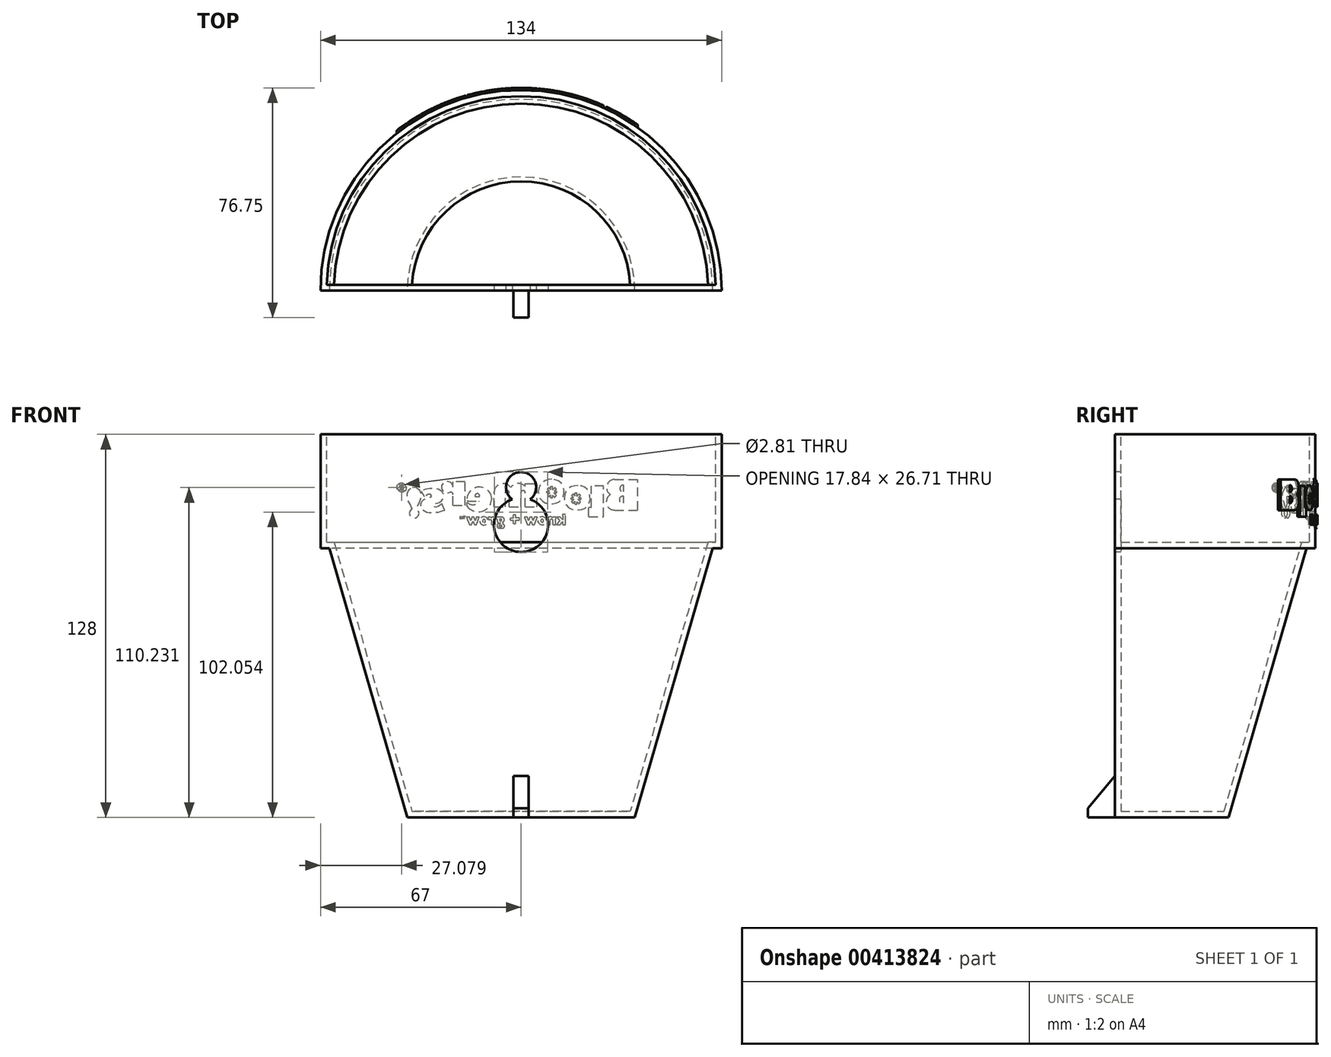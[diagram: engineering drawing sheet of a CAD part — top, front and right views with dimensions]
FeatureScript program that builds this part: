
annotation { "Feature Type Name" : "Feature", "Feature Type Description" : "" }
export const myFeature = defineFeature(function(context is Context, id is Id, definition is map)
    precondition{}
    {
        {
            var Q0;
            Q0=qCreatedBy(makeId("Front.planeOp"),FACE);
            var sketch = newSketch(context, id + "F0", { "sketchPlane" : qUnion([Q0])});
            skLineSegment(sketch, "E0", {"start": v(0, 56.42) * mm, "end": v(-67, 56.42) * mm});
            skLineSegment(sketch, "E1", {"start": v(-67, 56.42) * mm, "end": v(-67, 18.42) * mm});
            skLineSegment(sketch, "E2", {"start": v(0, -71.58) * mm, "end": v(-38, -71.58) * mm});
            skLineSegment(sketch, "E3", {"start": v(-67, 18.42) * mm, "end": v(-64, 18.42) * mm});
            skLineSegment(sketch, "E4", {"start": v(0, 56.42) * mm, "end": v(0, -71.58) * mm});
            skLineSegment(sketch, "E5", {"start": v(-64, 18.42) * mm, "end": v(-38, -71.58) * mm});
            skLineSegment(sketch, "E6.MirrorCS", {"start": v(0, 56.42) * mm, "end": v(67, 56.42) * mm});
            skLineSegment(sketch, "E7.MirrorCS", {"start": v(67, 56.42) * mm, "end": v(67, 18.42) * mm});
            skLineSegment(sketch, "E8.MirrorCS", {"start": v(67, 18.42) * mm, "end": v(64, 18.42) * mm});
            skLineSegment(sketch, "E9.MirrorCS", {"start": v(64, 18.42) * mm, "end": v(38, -71.58) * mm});
            skLineSegment(sketch, "E10.MirrorCS", {"start": v(0, -71.58) * mm, "end": v(38, -71.58) * mm});
            skSolve(sketch);
        }
        {
            var Q0;
            {var subQ0=sQuery(id+"F0.wireOp",EDGE,"E3");Q0=makeQuery(id+"F0.imprint","IMPRINT",FACE,{"disambiguationData":[TD([[makeQuery(id+"F0.imprint","IMPRINT",EDGE,{"derivedFrom":subQ0}),1.0]])]});}
            var Q1;
            {var subQ1=sQuery(id+"F0.wireOp",EDGE,"E0");Q1=makeQuery(id+"F0.imprint","IMPRINT",FACE,{"disambiguationData":[TD([[makeQuery(id+"F0.imprint","IMPRINT",EDGE,{"derivedFrom":subQ1}),1.0]])]});}
            var Q2;
            Q2=makeQuery(id+"F0.imprint","IMPRINT",FACE,{"disambiguationData":[TD([[makeQuery(id+"F0.imprint","IMPRINT",EDGE,{"derivedFrom":sQuery(id+"F0.wireOp",EDGE,"Kfnrekvc-ZjTY-c2iQ-cK4z-hKnBe4uEAVNk")}),1.0]])]});
            var Q3;
            Q3=sQuery(id+"F0.wireOp",EDGE,"E4");
            revolve(context, id + "F1", {"entities" : qUnion([Q0, Q1, Q2]), "axis" : qUnion([Q3]), "revolveType" : RevolveType.ONE_DIRECTION, "angle" : 180 * degree});
        }
        {
            var Q0;
            Q0=makeQuery(id+"FK2OT3XlAi37Aaq_1.splitOp","SPLIT",FACE,{"derivedFrom":makeQuery(id+"F1.opRevolve","SWEPT_FACE",FACE,{"disambiguationData":[OSD([sQuery(id+"F0.wireOp",EDGE,"E0")])]}),"isFromBackBody":true});
            shell(context, id + "F2", {"entities" : qUnion([Q0]), "thickness" : 2 * mm});
        }
        {
            var Q0;
            Q0=qCreatedBy(makeId("Front.planeOp"),FACE);
            var sketch = newSketch(context, id + "F3", { "sketchPlane" : qUnion([Q0])});
            skLineSegment(sketch, "E11.bottom", {"start": v(-2.5, -56.58) * mm, "end": v(2.5, -56.58) * mm});
            skLineSegment(sketch, "E11.top", {"start": v(-2.5, -71.58) * mm, "end": v(2.5, -71.58) * mm});
            skLineSegment(sketch, "E11.left", {"start": v(-2.5, -56.58) * mm, "end": v(-2.5, -71.58) * mm});
            skLineSegment(sketch, "E11.right", {"start": v(2.5, -56.58) * mm, "end": v(2.5, -71.58) * mm});
            skPoint(sketch, "E11.middle", {"position": v(0, -64.08) * mm});
            skSolve(sketch);
        }
        {
            var Q0;
            Q0=qSketchRegion(id+"F3",true);
            extrude(context, id + "F4", {"entities" : qUnion([Q0]), "operationType" : NewBodyOperationType.ADD, "depth" : 9 * mm});
        }
        {
            var Q0;
            Q0=qCreatedBy(makeId("Front.planeOp"),FACE);
            var sketch = newSketch(context, id + "F5", { "sketchPlane" : qUnion([Q0])});
            skCircle(sketch, "E12", {"center": v(0, 38.78) * mm, "radius": 5.05 * mm});
            skCircle(sketch, "E13", {"center": v(0, 26.17) * mm, "radius": 9.05 * mm});
            skSolve(sketch);
        }
        {
            var Q0;
            {var subQ0=sQuery(id+"F5.wireOp",EDGE,"E13");var subQ1=sQuery(id+"F5.wireOp",EDGE,"E12");var subQ2=makeQuery(id+"F5.imprint","INTERSECT",VERTEX,{"disambiguationData":[OD(0.0)],"derivedFrom":[subQ1,subQ0]});Q0=makeQuery(id+"F5.imprint","IMPRINT",FACE,{"disambiguationData":[TD([[makeQuery(id+"F5.imprint","IMPRINT",EDGE,{"disambiguationData":[TD([[subQ2,1.0]])],"derivedFrom":subQ1}),1.0]])]});}
            var Q1;
            {var subQ0=sQuery(id+"F5.wireOp",EDGE,"E13");var subQ1=sQuery(id+"F5.wireOp",EDGE,"E12");var subQ2=makeQuery(id+"F5.imprint","INTERSECT",VERTEX,{"disambiguationData":[OD(0.0)],"derivedFrom":[subQ1,subQ0]});Q1=makeQuery(id+"F5.imprint","IMPRINT",FACE,{"disambiguationData":[TD([[makeQuery(id+"F5.imprint","IMPRINT",EDGE,{"disambiguationData":[TD([[subQ2,-1.0]])],"derivedFrom":subQ1}),-1.0]])]});}
            var Q2;
            {var subQ0=sQuery(id+"F5.wireOp",EDGE,"E13");var subQ1=sQuery(id+"F5.wireOp",EDGE,"E12");var subQ2=makeQuery(id+"F5.imprint","INTERSECT",VERTEX,{"disambiguationData":[OD(0.0)],"derivedFrom":[subQ1,subQ0]});Q2=makeQuery(id+"F5.imprint","IMPRINT",FACE,{"disambiguationData":[TD([[makeQuery(id+"F5.imprint","IMPRINT",EDGE,{"disambiguationData":[TD([[subQ2,-1.0]])],"derivedFrom":subQ1}),1.0]])]});}
            var Q3;
            Q3=sQuery(id+"F5.wireOp",EDGE,"E12");
            var Q4;
            Q4=sQuery(id+"F5.wireOp",EDGE,"E13");
            extrude(context, id + "F6", {"entities" : qUnion([Q0, Q1, Q2]), "operationType" : NewBodyOperationType.REMOVE, "surfaceEntities" : qUnion([Q3, Q4]), "oppositeDirection" : true, "depth" : 10 * mm});
        }
        {
            var Q0;
            Q0=makeQuery(id+"F4.opExtrude","CAP_EDGE",EDGE,{"disambiguationData":[OSD([sQuery(id+"F3.wireOp",EDGE,"E11.bottom")])],"isStart":false});
            chamfer(context, id + "F7", {"entities" : qUnion([Q0]), "chamferType" : ChamferType.OFFSET_ANGLE, "width" : 10 * mm, "oppositeDirection" : false, "angle" : 50 * degree, "tangentPropagation" : true});
        }
        {
            var Q0;
            Q0=makeQuery(id+"F2.opShell","OFFSET_FACE",FACE,{"disambiguationData":[OSD([sQuery(id+"F0.wireOp",EDGE,"E0"),sQuery(id+"F0.wireOp",EDGE,"E1"),sQuery(id+"F0.wireOp",EDGE,"E2"),sQuery(id+"F0.wireOp",EDGE,"E3"),sQuery(id+"F0.wireOp",EDGE,"E4"),sQuery(id+"F0.wireOp",EDGE,"E5")])]});
            cPlane(context, id + "F8", {"entities" : qUnion([Q0]), "cplaneType" : CPlaneType.OFFSET, "offset" : 66.8 * mm, "width" : 150 * mm, "height" : 150 * mm});
        }
        {
            var Q0;
            Q0=qCreatedBy(id+"F8.planeOp",FACE);
            var sketch = newSketch(context, id + "F9", { "sketchPlane" : qUnion([Q0])});
            skLineSegment(sketch, "E14", {"start": v(-38.93, 41.35) * mm, "end": v(-38.93, 31.1) * mm});
            skLineSegment(sketch, "E15", {"start": v(-38.93, 31.1) * mm, "end": v(-31.26, 31.1) * mm});
            skLineSegment(sketch, "E16", {"start": v(-38.93, 41.35) * mm, "end": v(-31.26, 41.35) * mm});
            skArc(sketch, "E17", {"start": v(-29.86, 36.3) * mm, "mid": v(-28.64, 39.36) * mm, "end": v(-31.26, 41.35) * mm});
            skArc(sketch, "E18", {"start": v(-31.26, 31.1) * mm, "mid": v(-28.56, 33.17) * mm, "end": v(-29.86, 36.3) * mm});
            skLineSegment(sketch, "E19", {"start": v(-34.3, 39.39) * mm, "end": v(-34.3, 37.24) * mm});
            skArc(sketch, "E20", {"start": v(-34.3, 37.24) * mm, "mid": v(-33, 38.32) * mm, "end": v(-34.3, 39.39) * mm});
            skArc(sketch, "E21", {"start": v(-34.3, 33.47) * mm, "mid": v(-32.82, 34.59) * mm, "end": v(-34.3, 35.7) * mm});
            skLineSegment(sketch, "E22.trimOffspring", {"start": v(-34.3, 35.7) * mm, "end": v(-34.3, 33.47) * mm});
            skLineSegment(sketch, "E23", {"start": v(-27.58, 39.2) * mm, "end": v(-27.58, 28.9) * mm});
            skLineSegment(sketch, "E24", {"start": v(-27.58, 28.9) * mm, "end": v(-22.58, 28.9) * mm});
            skLineSegment(sketch, "E25", {"start": v(-22.58, 28.9) * mm, "end": v(-22.58, 31.98) * mm});
            skLineSegment(sketch, "E26", {"start": v(-22.58, 31.98) * mm, "end": v(-23.52, 31.98) * mm});
            skLineSegment(sketch, "E27", {"start": v(-23.52, 31.98) * mm, "end": v(-23.52, 39.2) * mm});
            skLineSegment(sketch, "E28", {"start": v(-23.52, 39.2) * mm, "end": v(-27.58, 39.2) * mm});
            skFitSpline(sketch, "E29", {"points": [v(-18.97, 39.3) * mm, v(-20.87, 38.92) * mm, v(-22.46, 37.44) * mm, v(-22.99, 35.82) * mm, v(-22.97, 34.09) * mm, v(-22.03, 32.34) * mm, v(-20.21, 31.27) * mm, v(-18.57, 31.14) * mm, v(-16.6, 31.5) * mm, v(-14.9, 33.15) * mm, v(-14.42, 35.37) * mm, v(-14.96, 37.3) * mm, v(-16.45, 38.75) * mm, v(-18.2, 39.28) * mm, v(-18.97, 39.3) * mm]});
            skLineSegment(sketch, "E30.bottom", {"start": v(-18.65, 36.9) * mm, "end": v(-18, 36.9) * mm});
            skLineSegment(sketch, "E30.top", {"start": v(-18.65, 33.13) * mm, "end": v(-18, 33.13) * mm});
            skLineSegment(sketch, "E30.left", {"start": v(-18.65, 36.9) * mm, "end": v(-18.65, 35.74) * mm});
            skLineSegment(sketch, "E30.right", {"start": v(-18, 36.9) * mm, "end": v(-18, 35.82) * mm});
            skLineSegment(sketch, "E31.bottom", {"start": v(-20.04, 35.3) * mm, "end": v(-19.23, 35.3) * mm});
            skLineSegment(sketch, "E31.top", {"start": v(-20.04, 34.7) * mm, "end": v(-19.05, 34.7) * mm});
            skLineSegment(sketch, "E31.left", {"start": v(-20.04, 35.3) * mm, "end": v(-20.04, 34.7) * mm});
            skLineSegment(sketch, "E31.right", {"start": v(-16.69, 35.3) * mm, "end": v(-16.69, 34.7) * mm});
            skLineSegment(sketch, "E32", {"start": v(-19.87, 35.97) * mm, "end": v(-19.23, 35.3) * mm});
            skLineSegment(sketch, "E33", {"start": v(-17.4, 33.43) * mm, "end": v(-16.88, 33.92) * mm});
            skLineSegment(sketch, "E34", {"start": v(-19.35, 36.45) * mm, "end": v(-19.87, 35.97) * mm});
            skLineSegment(sketch, "E35", {"start": v(-19.87, 33.85) * mm, "end": v(-19.25, 33.22) * mm});
            skLineSegment(sketch, "E36", {"start": v(-19.25, 33.22) * mm, "end": v(-18.65, 33.9) * mm});
            skLineSegment(sketch, "E37", {"start": v(-16.84, 35.97) * mm, "end": v(-17.39, 36.45) * mm});
            skLineSegment(sketch, "E38", {"start": v(-17.39, 36.45) * mm, "end": v(-18, 35.82) * mm});
            skLineSegment(sketch, "E39.trimOffspring", {"start": v(-18.65, 35.74) * mm, "end": v(-19.35, 36.45) * mm});
            skLineSegment(sketch, "E40.trimOffspring", {"start": v(-19.05, 34.7) * mm, "end": v(-19.87, 33.85) * mm});
            skLineSegment(sketch, "E41.trimOffspring", {"start": v(-18, 34.04) * mm, "end": v(-17.4, 33.43) * mm});
            skLineSegment(sketch, "E42.trimOffspring", {"start": v(-18.65, 33.9) * mm, "end": v(-18.65, 33.13) * mm});
            skLineSegment(sketch, "E43.trimOffspring", {"start": v(-18, 34.04) * mm, "end": v(-18, 33.13) * mm});
            skLineSegment(sketch, "E44.trimOffspring", {"start": v(-17.42, 35.3) * mm, "end": v(-16.84, 35.97) * mm});
            skLineSegment(sketch, "E45.trimOffspring", {"start": v(-17.42, 35.3) * mm, "end": v(-16.69, 35.3) * mm});
            skLineSegment(sketch, "E46.trimOffspring", {"start": v(-17.65, 34.7) * mm, "end": v(-16.69, 34.7) * mm});
            skFitSpline(sketch, "E47", {"points": [v(-10.3, 41.42) * mm, v(-12.2, 41.04) * mm, v(-13.79, 39.56) * mm, v(-14.32, 37.94) * mm, v(-14.3, 36.2) * mm, v(-13.36, 34.46) * mm, v(-11.55, 33.39) * mm, v(-9.9, 33.26) * mm, v(-7.94, 33.62) * mm, v(-6.23, 35.27) * mm, v(-5.76, 37.49) * mm, v(-6.3, 39.41) * mm, v(-7.79, 40.86) * mm, v(-9.54, 41.4) * mm, v(-10.3, 41.42) * mm]});
            skLineSegment(sketch, "E48", {"start": v(-17.65, 34.7) * mm, "end": v(-16.88, 33.92) * mm});
            skLineSegment(sketch, "E49.bottom", {"start": v(-10.58, 39.06) * mm, "end": v(-9.92, 39.06) * mm});
            skLineSegment(sketch, "E49.top", {"start": v(-10.58, 35.28) * mm, "end": v(-9.92, 35.28) * mm});
            skLineSegment(sketch, "E49.left", {"start": v(-10.58, 39.06) * mm, "end": v(-10.58, 37.9) * mm});
            skLineSegment(sketch, "E49.right", {"start": v(-9.92, 39.06) * mm, "end": v(-9.92, 37.97) * mm});
            skLineSegment(sketch, "E50.bottom", {"start": v(-11.97, 37.46) * mm, "end": v(-11.15, 37.46) * mm});
            skLineSegment(sketch, "E50.top", {"start": v(-11.97, 36.86) * mm, "end": v(-10.98, 36.86) * mm});
            skLineSegment(sketch, "E50.left", {"start": v(-11.97, 37.46) * mm, "end": v(-11.97, 36.86) * mm});
            skLineSegment(sketch, "E50.right", {"start": v(-8.61, 37.46) * mm, "end": v(-8.61, 36.86) * mm});
            skLineSegment(sketch, "E51", {"start": v(-11.8, 38.12) * mm, "end": v(-11.15, 37.46) * mm});
            skLineSegment(sketch, "E52", {"start": v(-9.32, 35.58) * mm, "end": v(-8.81, 36.08) * mm});
            skLineSegment(sketch, "E53", {"start": v(-11.27, 38.6) * mm, "end": v(-11.8, 38.12) * mm});
            skLineSegment(sketch, "E54", {"start": v(-11.8, 36) * mm, "end": v(-11.18, 35.37) * mm});
            skLineSegment(sketch, "E55", {"start": v(-11.18, 35.37) * mm, "end": v(-10.58, 36.05) * mm});
            skLineSegment(sketch, "E56", {"start": v(-8.76, 38.12) * mm, "end": v(-9.31, 38.6) * mm});
            skLineSegment(sketch, "E57", {"start": v(-9.31, 38.6) * mm, "end": v(-9.92, 37.97) * mm});
            skLineSegment(sketch, "E58.trimOffspring", {"start": v(-10.58, 37.9) * mm, "end": v(-11.27, 38.6) * mm});
            skLineSegment(sketch, "E59.trimOffspring", {"start": v(-10.98, 36.86) * mm, "end": v(-11.8, 36) * mm});
            skLineSegment(sketch, "E60.trimOffspring", {"start": v(-9.92, 36.2) * mm, "end": v(-9.32, 35.58) * mm});
            skLineSegment(sketch, "E61.trimOffspring", {"start": v(-10.58, 36.05) * mm, "end": v(-10.58, 35.28) * mm});
            skLineSegment(sketch, "E62.trimOffspring", {"start": v(-9.92, 36.2) * mm, "end": v(-9.92, 35.28) * mm});
            skLineSegment(sketch, "E63.trimOffspring", {"start": v(-9.34, 37.46) * mm, "end": v(-8.76, 38.12) * mm});
            skLineSegment(sketch, "E64.trimOffspring", {"start": v(-9.34, 37.46) * mm, "end": v(-8.61, 37.46) * mm});
            skLineSegment(sketch, "E65.trimOffspring", {"start": v(-9.58, 36.86) * mm, "end": v(-8.61, 36.86) * mm});
            skLineSegment(sketch, "E66", {"start": v(-9.58, 36.86) * mm, "end": v(-8.81, 36.08) * mm});
            skLineSegment(sketch, "E67", {"start": v(-5.38, 32.17) * mm, "end": v(-5.38, 39.97) * mm});
            skLineSegment(sketch, "E68", {"start": v(-5.38, 39.97) * mm, "end": v(-1.39, 39.97) * mm});
            skLineSegment(sketch, "E69", {"start": v(-1.39, 39.97) * mm, "end": v(-1.39, 39) * mm});
            skLineSegment(sketch, "E70", {"start": v(-5.38, 32.17) * mm, "end": v(-1.38, 32.17) * mm});
            skLineSegment(sketch, "E71", {"start": v(-1.38, 32.17) * mm, "end": v(-1.38, 36.98) * mm});
            skLineSegment(sketch, "E72", {"start": v(0, 36.98) * mm, "end": v(0, 32.17) * mm});
            skLineSegment(sketch, "E73", {"start": v(0, 32.17) * mm, "end": v(3.95, 32.17) * mm});
            skLineSegment(sketch, "E74", {"start": v(3.95, 32.17) * mm, "end": v(3.95, 36.98) * mm});
            skLineSegment(sketch, "E75", {"start": v(5.25, 36.98) * mm, "end": v(5.25, 32.17) * mm});
            skLineSegment(sketch, "E76", {"start": v(5.25, 32.17) * mm, "end": v(9.02, 32.17) * mm});
            skLineSegment(sketch, "E77", {"start": v(9.02, 32.17) * mm, "end": v(9.02, 36.98) * mm});
            skArc(sketch, "E78", {"start": v(5.25, 36.98) * mm, "mid": v(4.6, 37.63) * mm, "end": v(3.95, 36.98) * mm});
            skArc(sketch, "E79", {"start": v(0, 36.98) * mm, "mid": v(-0.69, 37.67) * mm, "end": v(-1.38, 36.98) * mm});
            skArc(sketch, "E80", {"start": v(3.53, 38.66) * mm, "mid": v(1.15, 40.01) * mm, "end": v(-1.39, 39) * mm});
            skArc(sketch, "E81", {"start": v(9.02, 36.98) * mm, "mid": v(6.9, 39.85) * mm, "end": v(3.53, 38.66) * mm});
            skArc(sketch, "E82", {"start": v(13.95, 34.1) * mm, "mid": v(15.9, 32.9) * mm, "end": v(18.03, 33.72) * mm});
            skArc(sketch, "E83", {"start": v(9.77, 35.2) * mm, "mid": v(12.91, 30.78) * mm, "end": v(18.06, 32.5) * mm});
            skArc(sketch, "E84", {"start": v(18.03, 34.17) * mm, "mid": v(14.4, 38.8) * mm, "end": v(9.77, 35.2) * mm});
            skLineSegment(sketch, "E85", {"start": v(13.95, 34.1) * mm, "end": v(18.03, 34.17) * mm});
            skLineSegment(sketch, "E86", {"start": v(13.9, 35.57) * mm, "end": v(15.36, 35.6) * mm});
            skArc(sketch, "E87", {"start": v(15.36, 35.6) * mm, "mid": v(14.6, 36.63) * mm, "end": v(13.9, 35.57) * mm});
            skLineSegment(sketch, "E88", {"start": v(18.03, 33.72) * mm, "end": v(18.06, 32.5) * mm});
            skLineSegment(sketch, "E89", {"start": v(22.73, 38.77) * mm, "end": v(22.73, 40.55) * mm});
            skLineSegment(sketch, "E90", {"start": v(22.73, 40.55) * mm, "end": v(18.72, 40.58) * mm});
            skLineSegment(sketch, "E91", {"start": v(18.72, 40.58) * mm, "end": v(18.72, 32.74) * mm});
            skLineSegment(sketch, "E92", {"start": v(18.72, 32.74) * mm, "end": v(22.7, 32.74) * mm});
            skLineSegment(sketch, "E93", {"start": v(22.7, 32.74) * mm, "end": v(22.7, 36.3) * mm});
            skArc(sketch, "E94", {"start": v(23.94, 36.98) * mm, "mid": v(26.24, 39.84) * mm, "end": v(22.73, 38.77) * mm});
            skArc(sketch, "E95", {"start": v(23.94, 36.98) * mm, "mid": v(23.11, 37) * mm, "end": v(22.7, 36.3) * mm});
            skLineSegment(sketch, "E96", {"start": v(33.3, 37.45) * mm, "end": v(32.27, 35.62) * mm});
            skFitSpline(sketch, "E97", {"points": [v(33.3, 37.45) * mm, v(32.36, 37.96) * mm, v(31.25, 38.2) * mm, v(30.16, 38.3) * mm, v(28.65, 38.26) * mm, v(27.14, 37.83) * mm, v(26.29, 37.06) * mm, v(25.86, 36.05) * mm, v(26.07, 34.84) * mm, v(26.79, 33.99) * mm, v(28.33, 33.35) * mm, v(29.12, 33.1) * mm, v(29.36, 32.85) * mm, v(29.3, 32.47) * mm, v(29, 32.12) * mm, v(28.48, 32.1) * mm, v(27.57, 32.38) * mm, v(26.88, 32.96) * mm, v(26.6, 33.22) * mm, v(26.49, 33.3) * mm], "startDerivative": vector(-15.65, 9.87) * mm, "endDerivative": vector(-4.84, 3.4) * mm});
            skFitSpline(sketch, "E98", {"points": [v(32.27, 35.62) * mm, v(31.94, 35.79) * mm, v(31.56, 36.06) * mm, v(31.13, 36.28) * mm, v(30.73, 36.4) * mm, v(30.1, 36.28) * mm, v(29.89, 35.88) * mm, v(30.08, 35.62) * mm, v(30.64, 35.32) * mm, v(31.42, 35.1) * mm, v(32.1, 34.87) * mm, v(32.63, 34.52) * mm, v(33.07, 34.09) * mm, v(33.37, 33.46) * mm, v(33.46, 33) * mm, v(33.46, 32.48) * mm, v(33.31, 31.72) * mm, v(32.8, 31.07) * mm, v(32.27, 30.71) * mm, v(31.46, 30.26) * mm, v(30.44, 30.1) * mm, v(29.25, 30.17) * mm, v(28.56, 30.21) * mm, v(27.53, 30.4) * mm, v(26.65, 30.67) * mm, v(26.13, 30.83) * mm, v(25.52, 31) * mm, v(24, 31.52) * mm], "startDerivative": vector(-12.22, 5.14) * mm, "endDerivative": vector(-29.8, 10.92) * mm});
            skLineSegment(sketch, "E99", {"start": v(26.49, 33.3) * mm, "end": v(25.52, 31) * mm});
            skFitSpline(sketch, "E100", {"points": [v(35.16, 31.53) * mm, v(34.54, 32.68) * mm, v(33.94, 33.8) * mm, v(33.6, 34.86) * mm, v(33.49, 36.06) * mm, v(33.7, 37.34) * mm, v(34.55, 38.4) * mm, v(35.36, 38.83) * mm, v(36.02, 38.89) * mm, v(36.86, 38.44) * mm, v(37.6, 37.54) * mm, v(38.02, 36.55) * mm, v(37.98, 35.4) * mm, v(37.68, 34.14) * mm, v(37.17, 33.21) * mm, v(36.7, 32.27) * mm, v(36.3, 31.56) * mm, v(36.34, 31.34) * mm], "startDerivative": vector(-9.25, 17.51) * mm, "endDerivative": vector(7.08, -5.7) * mm});
            skFitSpline(sketch, "E101", {"points": [v(35.16, 31.53) * mm, v(34.67, 31.23) * mm, v(34.3, 30.83) * mm, v(34.1, 30) * mm, v(34.28, 29.4) * mm, v(34.62, 28.94) * mm, v(35.02, 28.64) * mm, v(35.5, 28.5) * mm, v(36.33, 28.63) * mm, v(37.12, 29.37) * mm, v(37.32, 30.35) * mm, v(37.03, 31) * mm, v(36.66, 31.33) * mm, v(36.3, 31.56) * mm], "startDerivative": vector(-7.2, -4.04) * mm, "endDerivative": vector(-5.92, 3.66) * mm});
            skLineSegment(sketch, "E102", {"start": v(-13.86, 29.67) * mm, "end": v(-14.85, 29.67) * mm});
            skLineSegment(sketch, "E103", {"start": v(-14.85, 29.67) * mm, "end": v(-14.85, 26.29) * mm});
            skLineSegment(sketch, "E104", {"start": v(-14.85, 26.29) * mm, "end": v(-13.95, 26.29) * mm});
            skLineSegment(sketch, "E105", {"start": v(-13.95, 26.29) * mm, "end": v(-13.95, 27.28) * mm});
            skLineSegment(sketch, "E106", {"start": v(-13.95, 27.28) * mm, "end": v(-13.01, 26.29) * mm});
            skLineSegment(sketch, "E107", {"start": v(-13.01, 26.29) * mm, "end": v(-11.85, 26.29) * mm});
            skLineSegment(sketch, "E108", {"start": v(-11.85, 26.29) * mm, "end": v(-12.9, 27.58) * mm});
            skLineSegment(sketch, "E109", {"start": v(-12.9, 27.58) * mm, "end": v(-11.98, 28.72) * mm});
            skLineSegment(sketch, "E110", {"start": v(-11.98, 28.72) * mm, "end": v(-13.1, 28.72) * mm});
            skLineSegment(sketch, "E111", {"start": v(-13.1, 28.72) * mm, "end": v(-13.95, 27.88) * mm});
            skLineSegment(sketch, "E112", {"start": v(-13.95, 27.88) * mm, "end": v(-13.86, 29.67) * mm});
            skLineSegment(sketch, "E113", {"start": v(-11.59, 26.29) * mm, "end": v(-10.62, 26.29) * mm});
            skLineSegment(sketch, "E114", {"start": v(-10.62, 26.29) * mm, "end": v(-10.62, 27.77) * mm});
            skLineSegment(sketch, "E115", {"start": v(-9.77, 27.88) * mm, "end": v(-9.77, 26.29) * mm});
            skLineSegment(sketch, "E116", {"start": v(-9.77, 26.29) * mm, "end": v(-8.9, 26.29) * mm});
            skLineSegment(sketch, "E117", {"start": v(-8.9, 26.29) * mm, "end": v(-8.95, 28.42) * mm});
            skLineSegment(sketch, "E118", {"start": v(-10.49, 28.6) * mm, "end": v(-10.62, 28.6) * mm});
            skLineSegment(sketch, "E119", {"start": v(-10.62, 28.6) * mm, "end": v(-10.62, 28.76) * mm});
            skLineSegment(sketch, "E120", {"start": v(-10.62, 28.76) * mm, "end": v(-11.61, 28.76) * mm});
            skLineSegment(sketch, "E121", {"start": v(-11.61, 28.76) * mm, "end": v(-11.59, 26.29) * mm});
            skEllipse(sketch, "E122", {"center": v(-7.04, 27.54) * mm, "majorRadius": 0.56 * mm, "minorRadius": 0.44 * mm, "majorAxis": v(0, -1)});
            skEllipse(sketch, "E123", {"center": v(-7.04, 27.54) * mm, "majorRadius": 1.33 * mm, "minorRadius": 1.47 * mm, "majorAxis": v(0.05, -1)});
            skLineSegment(sketch, "E124", {"start": v(-4.42, 28.79) * mm, "end": v(-5.45, 28.79) * mm});
            skLineSegment(sketch, "E125", {"start": v(-5.45, 28.79) * mm, "end": v(-4.45, 26.23) * mm});
            skLineSegment(sketch, "E126", {"start": v(-4.45, 26.23) * mm, "end": v(-3.77, 26.23) * mm});
            skLineSegment(sketch, "E127", {"start": v(-3.77, 26.23) * mm, "end": v(-3.28, 27.38) * mm});
            skLineSegment(sketch, "E128", {"start": v(-3.28, 27.38) * mm, "end": v(-2.82, 26.22) * mm});
            skLineSegment(sketch, "E129", {"start": v(-2.82, 26.22) * mm, "end": v(-2.1, 26.22) * mm});
            skLineSegment(sketch, "E130", {"start": v(-2.1, 26.22) * mm, "end": v(-1.1, 28.75) * mm});
            skLineSegment(sketch, "E131", {"start": v(-1.1, 28.75) * mm, "end": v(-2.15, 28.75) * mm});
            skLineSegment(sketch, "E132", {"start": v(-2.15, 28.75) * mm, "end": v(-2.48, 27.64) * mm});
            skLineSegment(sketch, "E133", {"start": v(-2.48, 27.64) * mm, "end": v(-2.9, 28.75) * mm});
            skLineSegment(sketch, "E134", {"start": v(-2.9, 28.75) * mm, "end": v(-3.65, 28.75) * mm});
            skLineSegment(sketch, "E135", {"start": v(-3.65, 28.75) * mm, "end": v(-4.02, 27.66) * mm});
            skLineSegment(sketch, "E136", {"start": v(-4.02, 27.66) * mm, "end": v(-4.42, 28.79) * mm});
            skLineSegment(sketch, "E137", {"start": v(2.5, 29.58) * mm, "end": v(1.8, 29.58) * mm});
            skLineSegment(sketch, "E138", {"start": v(1.8, 29.58) * mm, "end": v(1.8, 28.47) * mm});
            skLineSegment(sketch, "E139", {"start": v(1.8, 28.47) * mm, "end": v(0.59, 28.47) * mm});
            skLineSegment(sketch, "E140", {"start": v(0.59, 28.47) * mm, "end": v(0.59, 27.74) * mm});
            skLineSegment(sketch, "E141", {"start": v(0.59, 27.74) * mm, "end": v(1.77, 27.74) * mm});
            skLineSegment(sketch, "E142", {"start": v(1.77, 27.74) * mm, "end": v(1.77, 26.58) * mm});
            skLineSegment(sketch, "E143", {"start": v(1.77, 26.58) * mm, "end": v(2.5, 26.58) * mm});
            skLineSegment(sketch, "E144", {"start": v(2.5, 26.58) * mm, "end": v(2.5, 27.74) * mm});
            skLineSegment(sketch, "E145", {"start": v(2.5, 27.74) * mm, "end": v(3.63, 27.74) * mm});
            skLineSegment(sketch, "E146", {"start": v(3.63, 27.74) * mm, "end": v(3.63, 28.45) * mm});
            skLineSegment(sketch, "E147", {"start": v(3.63, 28.45) * mm, "end": v(2.5, 28.45) * mm});
            skLineSegment(sketch, "E148", {"start": v(2.5, 28.45) * mm, "end": v(2.5, 29.58) * mm});
            skEllipse(sketch, "E149", {"center": v(12.37, 27.5) * mm, "majorRadius": 0.56 * mm, "minorRadius": 0.47 * mm, "majorAxis": v(0, -1)});
            skEllipse(sketch, "E150", {"center": v(12.37, 27.5) * mm, "majorRadius": 1.38 * mm, "minorRadius": 1.44 * mm, "majorAxis": v(0, -1)});
            skEllipse(sketch, "E151", {"center": v(6.82, 27.81) * mm, "majorRadius": 0.35 * mm, "minorRadius": 0.38 * mm, "majorAxis": v(0, -1)});
            skEllipse(sketch, "E152", {"center": v(6.86, 25.77) * mm, "majorRadius": 0.5 * mm, "minorRadius": 0.27 * mm, "majorAxis": v(1, 0)});
            skLineSegment(sketch, "E153", {"start": v(9.75, 28.76) * mm, "end": v(8.72, 28.76) * mm});
            skLineSegment(sketch, "E154", {"start": v(8.72, 28.76) * mm, "end": v(8.72, 26.23) * mm});
            skLineSegment(sketch, "E155", {"start": v(8.72, 26.23) * mm, "end": v(9.77, 26.23) * mm});
            skLineSegment(sketch, "E156", {"start": v(9.77, 26.23) * mm, "end": v(9.77, 27.57) * mm});
            skLineSegment(sketch, "E157", {"start": v(16.42, 28.76) * mm, "end": v(15.75, 28.76) * mm});
            skLineSegment(sketch, "E158", {"start": v(15.75, 28.76) * mm, "end": v(15.33, 27.62) * mm});
            skLineSegment(sketch, "E159", {"start": v(15.33, 27.62) * mm, "end": v(14.91, 28.77) * mm});
            skLineSegment(sketch, "E160", {"start": v(14.91, 28.77) * mm, "end": v(14, 28.77) * mm});
            skLineSegment(sketch, "E161", {"start": v(14, 28.77) * mm, "end": v(14.91, 26.25) * mm});
            skLineSegment(sketch, "E162", {"start": v(14.91, 26.25) * mm, "end": v(15.58, 26.25) * mm});
            skLineSegment(sketch, "E163", {"start": v(15.58, 26.25) * mm, "end": v(16.06, 27.35) * mm});
            skLineSegment(sketch, "E164", {"start": v(16.06, 27.35) * mm, "end": v(16.6, 26.24) * mm});
            skLineSegment(sketch, "E165", {"start": v(16.6, 26.24) * mm, "end": v(17.25, 26.24) * mm});
            skLineSegment(sketch, "E166", {"start": v(17.25, 26.24) * mm, "end": v(18.26, 28.77) * mm});
            skLineSegment(sketch, "E167", {"start": v(18.26, 28.77) * mm, "end": v(17.24, 28.77) * mm});
            skLineSegment(sketch, "E168", {"start": v(17.24, 28.77) * mm, "end": v(16.82, 27.63) * mm});
            skLineSegment(sketch, "E169", {"start": v(16.82, 27.63) * mm, "end": v(16.42, 28.76) * mm});
            skArc(sketch, "E170", {"start": v(-9.77, 27.88) * mm, "mid": v(-10.23, 28.08) * mm, "end": v(-10.62, 27.77) * mm});
            skArc(sketch, "E171", {"start": v(-8.95, 28.42) * mm, "mid": v(-9.68, 28.85) * mm, "end": v(-10.49, 28.6) * mm});
            skLineSegment(sketch, "E172", {"start": v(9.75, 28.76) * mm, "end": v(9.75, 28.32) * mm});
            skLineSegment(sketch, "E173", {"start": v(10.97, 28.72) * mm, "end": v(10.69, 27.75) * mm});
            skArc(sketch, "E174", {"start": v(10.97, 28.72) * mm, "mid": v(10.29, 28.75) * mm, "end": v(9.75, 28.32) * mm});
            skArc(sketch, "E175", {"start": v(10.69, 27.75) * mm, "mid": v(10.2, 27.84) * mm, "end": v(9.77, 27.57) * mm});
            skLineSegment(sketch, "E176", {"start": v(8.25, 28.14) * mm, "end": v(8.25, 28.77) * mm});
            skLineSegment(sketch, "E177", {"start": v(8.25, 28.77) * mm, "end": v(6.33, 28.77) * mm});
            skArc(sketch, "E178", {"start": v(6.33, 28.77) * mm, "mid": v(5.61, 27.95) * mm, "end": v(6.19, 27.03) * mm});
            skArc(sketch, "E179", {"start": v(6.83, 26.9) * mm, "mid": v(7.8, 27.15) * mm, "end": v(7.96, 28.14) * mm});
            skLineSegment(sketch, "E180", {"start": v(7.96, 28.14) * mm, "end": v(8.25, 28.14) * mm});
            skLineSegment(sketch, "E181", {"start": v(6.83, 26.9) * mm, "end": v(6.83, 26.6) * mm});
            skLineSegment(sketch, "E182", {"start": v(6.83, 26.6) * mm, "end": v(7.57, 26.6) * mm});
            skArc(sketch, "E183", {"start": v(6.19, 27.03) * mm, "mid": v(5.96, 26.73) * mm, "end": v(6.04, 26.36) * mm});
            skArc(sketch, "E184", {"start": v(6.04, 26.36) * mm, "mid": v(5.52, 25.75) * mm, "end": v(6.04, 25.14) * mm});
            skArc(sketch, "E185", {"start": v(7.57, 25.14) * mm, "mid": v(8.09, 25.87) * mm, "end": v(7.57, 26.6) * mm});
            skArc(sketch, "E186", {"start": v(6.04, 25.14) * mm, "mid": v(6.8, 25.03) * mm, "end": v(7.57, 25.14) * mm});
            skText(sketch, "E187", { "text": "TM", "fontName": "OpenSans-Regular.ttf"});
            skCircle(sketch, "E188", {"center": v(39.92, 38.65) * mm, "radius": 1.58 * mm});
            skCircle(sketch, "E189", {"center": v(39.92, 38.65) * mm, "radius": 1.4 * mm});
            const initialGuessF9  = {"E187": [0.0186, 0.02816, 1, 0, 0.0009]};
            skSetInitialGuess(sketch, initialGuessF9);
            skSolve(sketch);
        }
        {
            var Q0;
            Q0=qSketchRegion(id+"F9",true);
            extrude(context, id + "F10", {"entities" : qUnion([Q0]), "operationType" : NewBodyOperationType.ADD, "endBound" : BoundingType.UP_TO_NEXT, "oppositeDirection" : true, "depth" : 25 * mm});
        }
        {
            var Q0;
            Q0=qCreatedBy(id+"F8.planeOp",FACE);
            var sketch = newSketch(context, id + "F11", { "sketchPlane" : qUnion([Q0])});
            skText(sketch, "E190", { "text": "R", "fontName": "OpenSans-Regular.ttf"});
            const initialGuessF11  = {"E190": [0.03904, 0.03769, 1, 0, 0.0019]};
            skSetInitialGuess(sketch, initialGuessF11);
            skSolve(sketch);
        }
        {
            var Q0;
            Q0=qSketchRegion(id+"F11",true);
            extrude(context, id + "F12", {"entities" : qUnion([Q0]), "operationType" : NewBodyOperationType.ADD, "endBound" : BoundingType.UP_TO_NEXT, "oppositeDirection" : true, "depth" : 25 * mm});
        }
        {
            var Q0;
            Q0=makeQuery(id+"F1.opRevolve","SWEPT_FACE",FACE,{"disambiguationData":[OSD([sQuery(id+"F0.wireOp",EDGE,"E0")])]});
            var sketch = newSketch(context, id + "F13", { "sketchPlane" : qUnion([Q0])});
            skCircle(sketch, "E191", {"center": v(0, 0) * mm, "radius": 67.75 * mm});
            skCircle(sketch, "E192", {"center": v(0, 0) * mm, "radius": 91 * mm});
            skSolve(sketch);
        }
        {
            var Q0;
            Q0=qSketchRegion(id+"F13",true);
            extrude(context, id + "F14", {"entities" : qUnion([Q0]), "operationType" : NewBodyOperationType.REMOVE, "oppositeDirection" : true, "depth" : 124 * mm});
        }
    });
